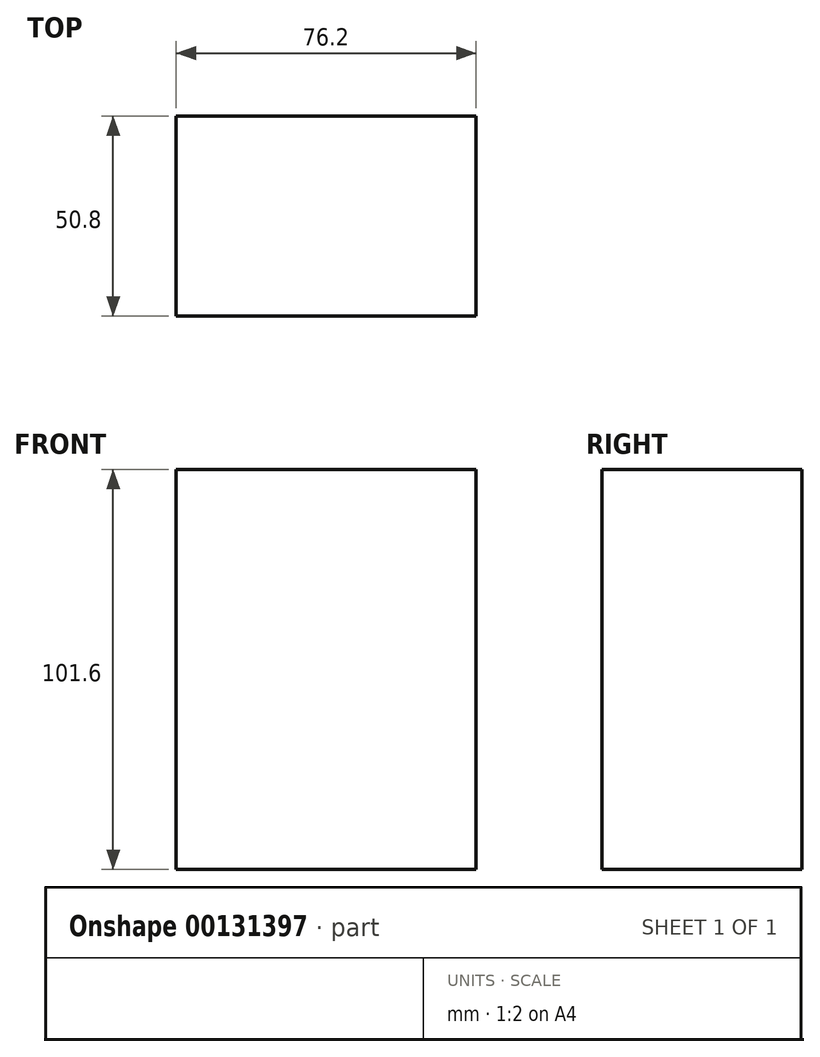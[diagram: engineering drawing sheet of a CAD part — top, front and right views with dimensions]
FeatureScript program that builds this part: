
annotation { "Feature Type Name" : "Feature", "Feature Type Description" : "" }
export const myFeature = defineFeature(function(context is Context, id is Id, definition is map)
    precondition{}
    {
        {
            var Q0;
            Q0=qCreatedBy(makeId("Top.planeOp"),FACE);
            var sketch = newSketch(context, id + "F0", { "sketchPlane" : qUnion([Q0])});
            skLineSegment(sketch, "E0.bottom", {"start": v(27.59, 25.4) * mm, "end": v(-48.61, 25.4) * mm});
            skLineSegment(sketch, "E0.top", {"start": v(27.59, -25.4) * mm, "end": v(-48.61, -25.4) * mm});
            skLineSegment(sketch, "E0.left", {"start": v(27.59, 25.4) * mm, "end": v(27.59, -25.4) * mm});
            skLineSegment(sketch, "E0.right", {"start": v(-48.61, 25.4) * mm, "end": v(-48.61, -25.4) * mm});
            skPoint(sketch, "E0.middle", {"position": v(-10.51, 0) * mm});
            skSolve(sketch);
        }
        {
            var Q0;
            Q0 = qSketchRegion(id + "F0", true);
            extrude(context, id + "F1", {"entities" : qUnion([Q0]), "depth" : 101.6 * mm});
        }
    });
